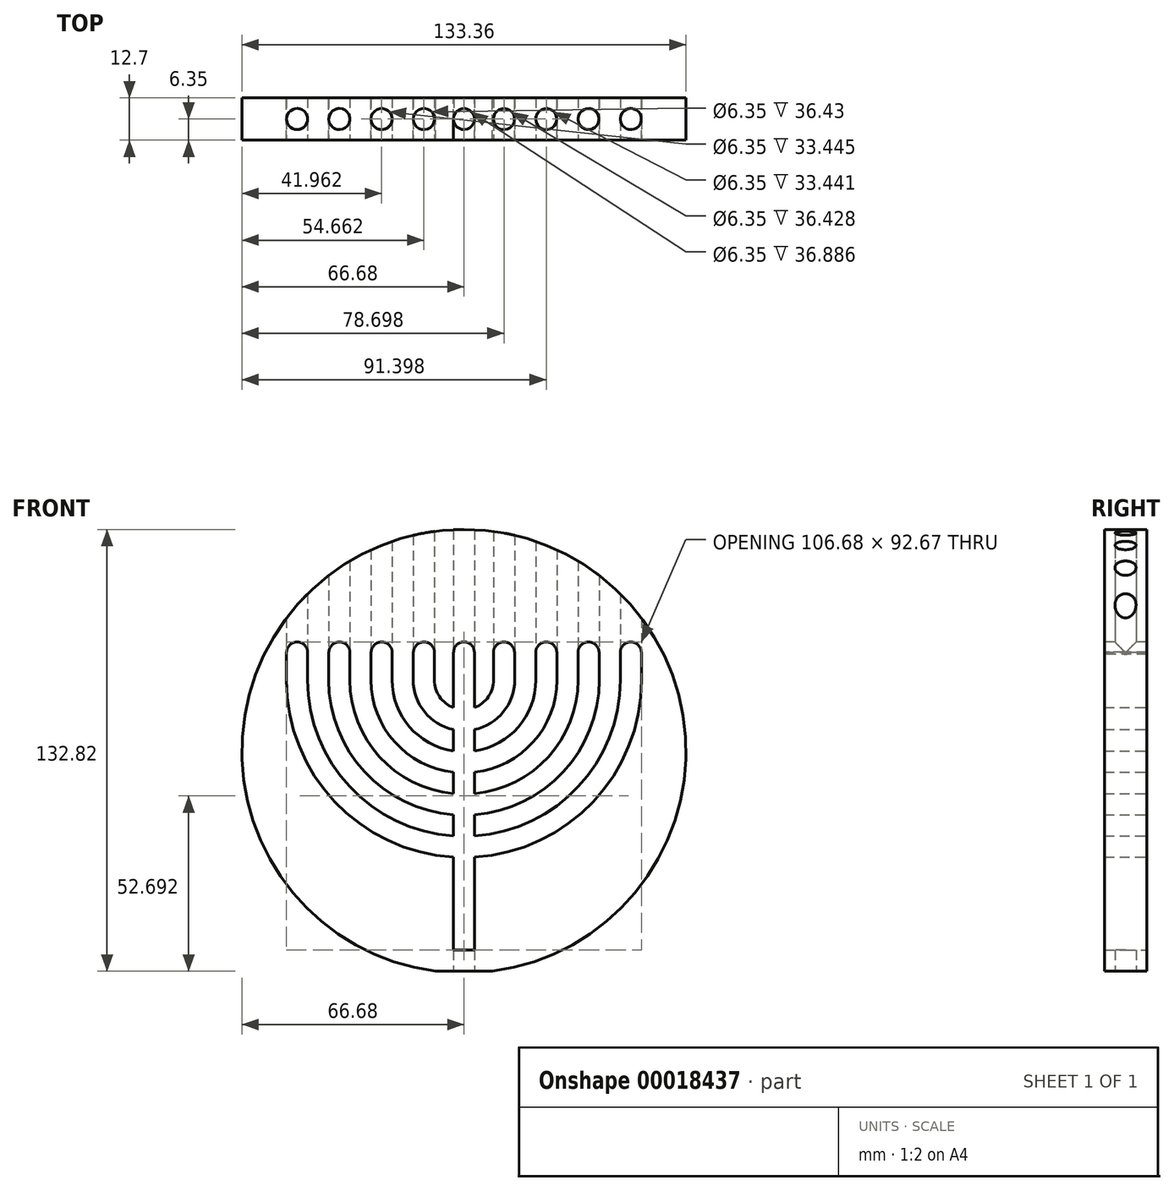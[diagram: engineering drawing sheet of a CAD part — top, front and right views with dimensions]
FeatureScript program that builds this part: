
annotation { "Feature Type Name" : "Feature", "Feature Type Description" : "" }
export const myFeature = defineFeature(function(context is Context, id is Id, definition is map)
    precondition{}
    {
        {
            var Q0;
            Q0=qCreatedBy(makeId("Front.planeOp"),FACE);
            var sketch = newSketch(context, id + "F0", { "sketchPlane" : qUnion([Q0])});
            skCircle(sketch, "E0", {"center": v(0, 0) * mm, "radius": 66.68 * mm});
            skSolve(sketch);
        }
        {
            var Q0;
            Q0 = qSketchRegion(id + "F0", true);
            extrude(context, id + "F1", {"entities" : qUnion([Q0]), "depth" : 12.7 * mm});
        }
        {
            var Q0;
            Q0=qCreatedBy(makeId("Front.planeOp"),FACE);
            var sketch = newSketch(context, id + "F2", { "sketchPlane" : qUnion([Q0])});
            skLineSegment(sketch, "E1.top", {"start": v(-3.17, -59.79) * mm, "end": v(3.17, -59.79) * mm});
            skLineSegment(sketch, "E1.left", {"start": v(-3.17, 29.79) * mm, "end": v(-3.17, 13.13) * mm});
            skLineSegment(sketch, "E1.right", {"start": v(3.18, 29.79) * mm, "end": v(3.18, 13.13) * mm});
            skArc(sketch, "E2", {"start": v(-53.34, 21.43) * mm, "mid": v(-38.82, -15.14) * mm, "end": v(-3.17, -31.81) * mm});
            skArc(sketch, "E3.0", {"start": v(-46.99, 21.43) * mm, "mid": v(-34.33, -10.65) * mm, "end": v(-3.17, -25.45) * mm});
            skArc(sketch, "E4.0", {"start": v(-40.64, 21.43) * mm, "mid": v(-29.84, -6.16) * mm, "end": v(-3.17, -19.08) * mm});
            skArc(sketch, "E5.0", {"start": v(-34.29, 21.43) * mm, "mid": v(-25.34, -1.66) * mm, "end": v(-3.17, -12.7) * mm});
            skArc(sketch, "E6.0", {"start": v(-27.94, 21.43) * mm, "mid": v(-20.85, 2.83) * mm, "end": v(-3.17, -6.32) * mm});
            skArc(sketch, "E7.0", {"start": v(-21.59, 21.43) * mm, "mid": v(-16.35, 7.34) * mm, "end": v(-3.17, 0.08) * mm});
            skArc(sketch, "E8.0", {"start": v(-15.24, 21.43) * mm, "mid": v(-11.85, 11.85) * mm, "end": v(-3.17, 6.53) * mm});
            skArc(sketch, "E9.0", {"start": v(-8.9, 21.43) * mm, "mid": v(-7.32, 16.4) * mm, "end": v(-3.17, 13.13) * mm});
            skLineSegment(sketch, "E10", {"start": v(8.9, 21.43) * mm, "end": v(8.9, 29.79) * mm});
            skLineSegment(sketch, "E11", {"start": v(15.24, 21.43) * mm, "end": v(15.24, 29.79) * mm});
            skLineSegment(sketch, "E12", {"start": v(21.59, 21.43) * mm, "end": v(21.59, 29.79) * mm});
            skLineSegment(sketch, "E13", {"start": v(27.94, 21.43) * mm, "end": v(27.94, 29.79) * mm});
            skLineSegment(sketch, "E14", {"start": v(34.29, 21.43) * mm, "end": v(34.29, 29.79) * mm});
            skLineSegment(sketch, "E15", {"start": v(40.64, 21.43) * mm, "end": v(40.64, 29.79) * mm});
            skLineSegment(sketch, "E16", {"start": v(46.99, 21.43) * mm, "end": v(46.99, 29.79) * mm});
            skLineSegment(sketch, "E17", {"start": v(53.34, 21.43) * mm, "end": v(53.34, 29.79) * mm});
            skLineSegment(sketch, "E18", {"start": v(53.34, 29.79) * mm, "end": v(46.99, 29.79) * mm});
            skLineSegment(sketch, "E19", {"start": v(-15.24, 21.43) * mm, "end": v(-15.24, 29.79) * mm});
            skLineSegment(sketch, "E20", {"start": v(-8.9, 21.43) * mm, "end": v(-8.9, 29.79) * mm});
            skLineSegment(sketch, "E21", {"start": v(-21.59, 21.43) * mm, "end": v(-21.59, 29.79) * mm});
            skLineSegment(sketch, "E22", {"start": v(-27.94, 21.43) * mm, "end": v(-27.94, 29.79) * mm});
            skLineSegment(sketch, "E23", {"start": v(-34.29, 21.43) * mm, "end": v(-34.29, 29.79) * mm});
            skLineSegment(sketch, "E24", {"start": v(-40.64, 21.43) * mm, "end": v(-40.64, 29.79) * mm});
            skLineSegment(sketch, "E25", {"start": v(-46.99, 21.43) * mm, "end": v(-46.99, 29.79) * mm});
            skLineSegment(sketch, "E26", {"start": v(-53.34, 21.43) * mm, "end": v(-53.34, 29.79) * mm});
            skLineSegment(sketch, "E27.trimOffspring", {"start": v(40.64, 29.79) * mm, "end": v(34.29, 29.79) * mm});
            skLineSegment(sketch, "E28.trimOffspring", {"start": v(27.94, 29.79) * mm, "end": v(21.59, 29.79) * mm});
            skLineSegment(sketch, "E29.trimOffspring", {"start": v(15.24, 29.79) * mm, "end": v(8.9, 29.79) * mm});
            skLineSegment(sketch, "E30.trimOffspring", {"start": v(-21.59, 29.79) * mm, "end": v(-27.94, 29.79) * mm});
            skLineSegment(sketch, "E31.trimOffspring", {"start": v(-34.29, 29.79) * mm, "end": v(-40.64, 29.79) * mm});
            skLineSegment(sketch, "E32.trimOffspring", {"start": v(-46.99, 29.79) * mm, "end": v(-53.34, 29.79) * mm});
            skLineSegment(sketch, "E33", {"start": v(-15.24, 29.79) * mm, "end": v(-8.9, 29.79) * mm});
            skLineSegment(sketch, "E34.trimOffspring", {"start": v(-3.17, 29.79) * mm, "end": v(3.18, 29.79) * mm});
            skArc(sketch, "E35.trimOffspring", {"start": v(3.17, 13.13) * mm, "mid": v(7.32, 16.4) * mm, "end": v(8.9, 21.43) * mm});
            skLineSegment(sketch, "E36.trimOffspring", {"start": v(3.18, 6.53) * mm, "end": v(3.18, 0.08) * mm});
            skLineSegment(sketch, "E37.trimOffspring", {"start": v(-3.17, 6.53) * mm, "end": v(-3.17, 0.08) * mm});
            skLineSegment(sketch, "E38.trimOffspring", {"start": v(-3.17, -6.32) * mm, "end": v(-3.17, -12.7) * mm});
            skArc(sketch, "E39.trimOffspring", {"start": v(3.18, 0.08) * mm, "mid": v(16.35, 7.34) * mm, "end": v(21.59, 21.43) * mm});
            skArc(sketch, "E40.trimOffspring", {"start": v(3.17, 6.53) * mm, "mid": v(11.85, 11.85) * mm, "end": v(15.24, 21.43) * mm});
            skLineSegment(sketch, "E41.trimOffspring", {"start": v(3.18, -6.32) * mm, "end": v(3.18, -12.7) * mm});
            skArc(sketch, "E42.trimOffspring", {"start": v(3.18, -6.32) * mm, "mid": v(20.85, 2.83) * mm, "end": v(27.94, 21.43) * mm});
            skArc(sketch, "E43.trimOffspring", {"start": v(3.17, -12.7) * mm, "mid": v(25.34, -1.66) * mm, "end": v(34.29, 21.43) * mm});
            skLineSegment(sketch, "E44.trimOffspring", {"start": v(3.18, -19.08) * mm, "end": v(3.18, -25.45) * mm});
            skLineSegment(sketch, "E45.trimOffspring", {"start": v(-3.17, -19.08) * mm, "end": v(-3.17, -25.45) * mm});
            skArc(sketch, "E46.trimOffspring", {"start": v(3.18, -19.08) * mm, "mid": v(29.84, -6.16) * mm, "end": v(40.64, 21.43) * mm});
            skLineSegment(sketch, "E47.trimOffspring", {"start": v(3.18, -31.81) * mm, "end": v(3.18, -59.79) * mm});
            skLineSegment(sketch, "E48.trimOffspring", {"start": v(-3.17, -31.81) * mm, "end": v(-3.17, -59.79) * mm});
            skArc(sketch, "E49.trimOffspring", {"start": v(3.17, -25.45) * mm, "mid": v(34.33, -10.65) * mm, "end": v(46.99, 21.43) * mm});
            skArc(sketch, "E50.trimOffspring", {"start": v(3.17, -31.81) * mm, "mid": v(38.82, -15.14) * mm, "end": v(53.34, 21.43) * mm});
            skLineSegment(sketch, "E51.bottom", {"start": v(-9.53, -66.14) * mm, "end": v(9.53, -66.14) * mm});
            skLineSegment(sketch, "E51.top", {"start": v(-9.53, -73.18) * mm, "end": v(9.53, -73.18) * mm});
            skLineSegment(sketch, "E51.left", {"start": v(-9.53, -66.14) * mm, "end": v(-9.53, -73.18) * mm});
            skLineSegment(sketch, "E51.right", {"start": v(9.53, -66.14) * mm, "end": v(9.53, -73.18) * mm});
            skSolve(sketch);
        }
        {
            var Q0;
            Q0 = qSketchRegion(id + "F2", true);
            var Q1;
            Q1=makeQuery(id+"F1.opExtrude","CAP_FACE",FACE,{"disambiguationData":[OSD([sQuery(id+"F0.wireOp",EDGE,"E0")])],"isStart":false});
            extrude(context, id + "F3", {"entities" : qUnion([Q0]), "operationType" : NewBodyOperationType.REMOVE, "endBound" : BoundingType.UP_TO_SURFACE, "endBoundEntityFace" : qUnion([Q1]), "depth" : 25.4 * mm});
        }
        {
            var Q0;
            Q0=qCreatedBy(makeId("Front.planeOp"),FACE);
            cPlane(context, id + "F4", {"entities" : qUnion([Q0]), "cplaneType" : CPlaneType.OFFSET, "offset" : 6.35 * mm, "width" : 152.4 * mm, "height" : 152.4 * mm});
        }
        {
            var Q0;
            Q0=qCreatedBy(id+"F4.planeOp",FACE);
            var sketch = newSketch(context, id + "F5", { "sketchPlane" : qUnion([Q0])});
            skCircle(sketch, "E52", {"center": v(-50.12, 29.66) * mm, "radius": 3.17 * mm});
            skCircle(sketch, "E53.1.0.0", {"center": v(-37.42, 29.66) * mm, "radius": 3.17 * mm});
            skCircle(sketch, "E53.2.0.0", {"center": v(-24.72, 29.66) * mm, "radius": 3.17 * mm});
            skCircle(sketch, "E53.3.0.0", {"center": v(-12.02, 29.66) * mm, "radius": 3.17 * mm});
            skLineSegment(sketch, "E53.direction1", {"start": v(-50.12, 29.66) * mm, "end": v(-37.42, 29.66) * mm, "construction": true});
            skCircle(sketch, "E54.MirrorC", {"center": v(12.02, 29.66) * mm, "radius": 3.17 * mm});
            skCircle(sketch, "E55.MirrorC", {"center": v(24.72, 29.66) * mm, "radius": 3.17 * mm});
            skCircle(sketch, "E56.MirrorC", {"center": v(37.42, 29.66) * mm, "radius": 3.17 * mm});
            skCircle(sketch, "E57.MirrorC", {"center": v(50.12, 29.66) * mm, "radius": 3.17 * mm});
            skCircle(sketch, "E58", {"center": v(0, 29.77) * mm, "radius": 3.11 * mm});
            skSolve(sketch);
        }
        {
            var Q0;
            Q0=qCreatedBy(makeId("Top.planeOp"),FACE);
            cPlane(context, id + "F6", {"entities" : qUnion([Q0]), "cplaneType" : CPlaneType.OFFSET, "offset" : 29.2 * mm, "width" : 152.4 * mm, "height" : 152.4 * mm});
        }
        {
            var Q0;
            Q0 = qSketchRegion(id + "F5", true);
            extrude(context, id + "F7", {"entities" : qUnion([Q0]), "operationType" : NewBodyOperationType.REMOVE, "oppositeDirection" : true, "depth" : 12.7 * mm, "hasSecondDirection" : true, "secondDirectionOppositeDirection" : false, "secondDirectionDepth" : 12.7 * mm});
        }
        {
            var Q0;
            Q0=qCreatedBy(id+"F6.planeOp",FACE);
            var sketch = newSketch(context, id + "F8", { "sketchPlane" : qUnion([Q0])});
            skPoint(sketch, "E59.0", {"position": v(-50.12, -6.35) * mm});
            skPoint(sketch, "E60.0", {"position": v(-37.42, -6.35) * mm});
            skPoint(sketch, "E61.0", {"position": v(-24.72, -6.35) * mm});
            skPoint(sketch, "E62.0", {"position": v(-12.02, -6.35) * mm});
            skPoint(sketch, "E63.0", {"position": v(0, -6.35) * mm});
            skPoint(sketch, "E64.0", {"position": v(12.02, -6.35) * mm});
            skPoint(sketch, "E65.0", {"position": v(24.72, -6.35) * mm});
            skPoint(sketch, "E66.0", {"position": v(37.42, -6.35) * mm});
            skPoint(sketch, "E67.0", {"position": v(50.12, -6.35) * mm});
            skCircle(sketch, "E68", {"center": v(-50.12, -6.35) * mm, "radius": 3.18 * mm});
            skCircle(sketch, "E69", {"center": v(-37.42, -6.35) * mm, "radius": 3.18 * mm});
            skCircle(sketch, "E70", {"center": v(-24.72, -6.35) * mm, "radius": 3.18 * mm});
            skCircle(sketch, "E71", {"center": v(-12.02, -6.35) * mm, "radius": 3.18 * mm});
            skCircle(sketch, "E72", {"center": v(0, -6.35) * mm, "radius": 3.18 * mm});
            skCircle(sketch, "E73", {"center": v(12.02, -6.35) * mm, "radius": 3.18 * mm});
            skCircle(sketch, "E74", {"center": v(24.72, -6.35) * mm, "radius": 3.18 * mm});
            skCircle(sketch, "E75", {"center": v(37.42, -6.35) * mm, "radius": 3.18 * mm});
            skCircle(sketch, "E76", {"center": v(50.12, -6.35) * mm, "radius": 3.18 * mm});
            skSolve(sketch);
        }
        {
            var Q0;
            Q0 = qSketchRegion(id + "F8", true);
            extrude(context, id + "F9", {"entities" : qUnion([Q0]), "operationType" : NewBodyOperationType.REMOVE, "endBound" : BoundingType.THROUGH_ALL, "depth" : 25.4 * mm});
        }
        {
            var Q0;
            Q0=makeQuery(id+"F3.boolean.opBoolean","COPY",FACE,{"derivedFrom":makeQuery(id+"F3.opExtrude","SWEPT_FACE",FACE,{"disambiguationData":[OSD([sQuery(id+"F2.wireOp",EDGE,"E51.bottom")])]})});
            var sketch = newSketch(context, id + "F10", { "sketchPlane" : qUnion([Q0])});
            skPoint(sketch, "E77.0", {"position": v(0, 6.35) * mm});
            skCircle(sketch, "E78", {"center": v(0, 6.35) * mm, "radius": 3.18 * mm});
            skSolve(sketch);
        }
        {
            var Q0;
            Q0=makeQuery(id+"F10.imprint","IMPRINT",FACE,{"disambiguationData":[TD([[makeQuery(id+"F10.imprint","IMPRINT",EDGE,{"derivedFrom":sQuery(id+"F10.wireOp",EDGE,"E78")}),1.0]])]});
            extrude(context, id + "F11", {"entities" : qUnion([Q0]), "operationType" : NewBodyOperationType.REMOVE, "oppositeDirection" : true, "depth" : 6.35 * mm});
        }
    });
